# Revit family: BISLEY_SystemFile_Drawer_Units
name_source: partatom
category: Furniture
revit_build: Autodesk Revit 2018 (Build: 20180423_1000(x64)
units: mm (PartAtom-declared; Revit-internal decimal feet)

## family parameters
Always vertical = Yes
Cut with Voids When Loaded = No
OmniClass Number = 23.40.20.00
OmniClass Title = General Furniture and Specialties
Room Calculation Point = No
Shared = No
Work Plane-Based = No

## types (12) — shared parameters
Category = Furniture
Compliance Standards Certification = BS EN 14073 2004 Part 2 & 3, BS EN 14074, BS 4875 1998 Part 7 level 4 & Part 8, BS 476 Part 7 1987 Class 2Y
Depth = 470 mm  [stored 1.54199 ft]
Finish = Powder Coated
Manufacturer = Bisley
Material = Steel
Name = Drawer Unit
Range = SystemFile
Routine Maintenance = We recommend you clean your unit with warm water and a mild detergent solution. A damp cloth can be used to remove dust particles.
URL = www.bisley.com
Uniclass 2015 Code = PR_40_30_25
Uniclass2015Title = Shelves and Storage Units
Uniclass2015Version = V1.1
Warranty = 10 Years

## per-type parameters (varying)
| type | Central Lock | Description | Drawer width1 | Drawer width2 | Height | Individual Locks | Model Reference | Number of drawers | Width |
| SYC08/0/2 | Yes | 2 Drawers and Counterbalance | 377 mm | -377 mm | 693 mm  [stored 2.27362 ft] | No | SYC08/0/2 | 2 | 800 mm  [stored 2.62467 ft] |
| SYC08/0/3 | Yes | 3 Drawers and Counterbalance | 377 mm | -377 mm | 997 mm | No | SYC08/0/3 | 3 | 800 mm  [stored 2.62467 ft] |
| SYC08/0/4 | Yes | 4 Drawers and Counterbalance | 377 mm | -377 mm | 1301 mm  [stored 4.26837 ft] | No | SYC08/0/4 | 4 | 800 mm  [stored 2.62467 ft] |
| SYC10/0/2 | Yes | 2 Drawers and Counterbalance | 477 mm | -477 mm | 693 mm  [stored 2.27362 ft] | No | SYC10/0/2 | 2 | 1000 mm  [stored 3.28084 ft] |
| SYC10/0/3 | Yes | 3 Drawers and Counterbalance | 477 mm | -477 mm | 997 mm | No | SYC10/0/3 | 3 | 1000 mm  [stored 3.28084 ft] |
| SYC10/0/4 | Yes | 4 Drawers and Counterbalance | 477 mm | -477 mm | 1301 mm  [stored 4.26837 ft] | No | SYC10/0/4 | 4 | 1000 mm  [stored 3.28084 ft] |
| SYCI08/20/0/2 | No | 2 drawers with securty divider plates | 377 mm | -377 mm | 693 mm  [stored 2.27362 ft] | Yes | SYCI08/20/0/2 | 2 | 800 mm  [stored 2.62467 ft] |
| SYCI08/30/0/3 | No | 3 drawers with security drawer divider plates | 377 mm | -377 mm | 997 mm | Yes | SYCI08/30/0/3 | 3 | 800 mm  [stored 2.62467 ft] |
| SYCI08/40/0/4 | No | 4 Drawers with security drawer divider plates | 377 mm | -377 mm | 1301 mm  [stored 4.26837 ft] | Yes | SYCI/40/0/4 | 4 | 800 mm  [stored 2.62467 ft] |
| SYCI10/20/0/2 | No | 2 drawers with security drawer divider plates | 477 mm | -477 mm | 693 mm  [stored 2.27362 ft] | Yes | SYCI10/20/0/2 | 2 | 1000 mm  [stored 3.28084 ft] |
| SYCI10/30/0/3 | No | 3 drawers with security drawer divider plates | 477 mm | -477 mm | 997 mm | Yes | SYCI10/30/0/3 | 3 | 1000 mm  [stored 3.28084 ft] |
| SYCI10/40/0/4 | No | 4 drawers with security drawer divider plates | 477 mm | -477 mm | 1301 mm  [stored 4.26837 ft] | Yes | SYCI10/40/0/4 | 4 | 1000 mm  [stored 3.28084 ft] |

note: [stored X ft] marks values corroborated as IEEE doubles in the binary element streams (Revit-internal decimal feet)

## geometry (parser evidence)
native form markers: Sweep x2
no freeform markers — native parametric forms only
